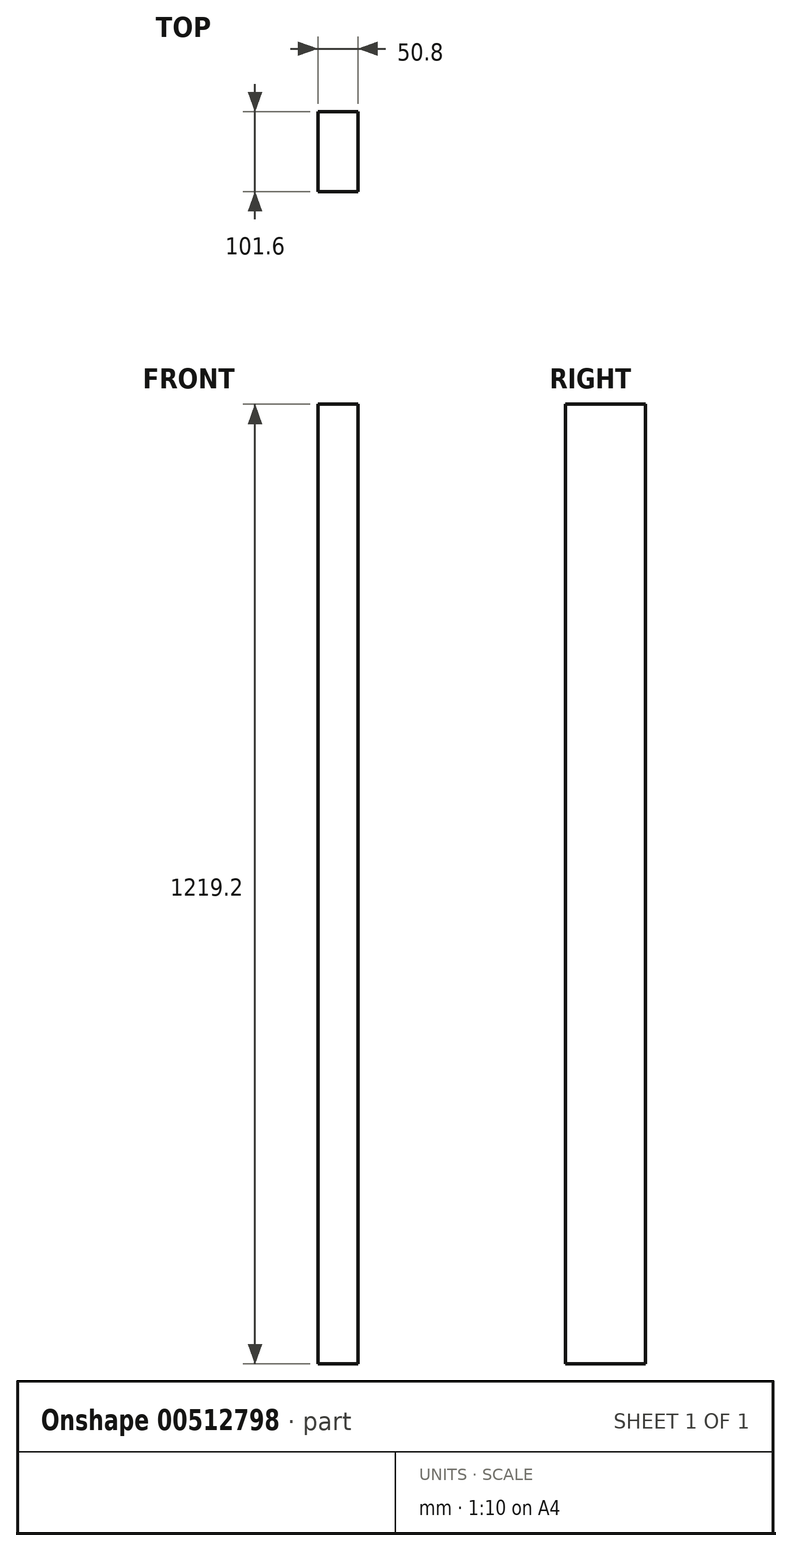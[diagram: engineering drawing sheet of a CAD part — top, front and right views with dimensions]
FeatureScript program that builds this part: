
annotation { "Feature Type Name" : "Feature", "Feature Type Description" : "" }
export const myFeature = defineFeature(function(context is Context, id is Id, definition is map)
    precondition{}
    {
        {
            var Q0;
            Q0=qCreatedBy(makeId("Top.planeOp"),FACE);
            var sketch = newSketch(context, id + "F0", { "sketchPlane" : qUnion([Q0])});
            skLineSegment(sketch, "E0.bottom", {"start": v(-25.4, 50.8) * mm, "end": v(25.4, 50.8) * mm});
            skLineSegment(sketch, "E0.top", {"start": v(-25.4, -50.8) * mm, "end": v(25.4, -50.8) * mm});
            skLineSegment(sketch, "E0.left", {"start": v(-25.4, 50.8) * mm, "end": v(-25.4, -50.8) * mm});
            skLineSegment(sketch, "E0.right", {"start": v(25.4, 50.8) * mm, "end": v(25.4, -50.8) * mm});
            skPoint(sketch, "E0.middle", {"position": v(0, 0) * mm});
            skSolve(sketch);
        }
        {
            var Q0;
            Q0=makeQuery(id+"F0.imprint","IMPRINT",FACE,{"disambiguationData":[TD([[makeQuery(id+"F0.imprint","IMPRINT",EDGE,{"derivedFrom":sQuery(id+"F0.wireOp",EDGE,"E0.bottom")}),-1.0]])]});
            extrude(context, id + "F1", {"entities" : qUnion([Q0]), "depth" : 1219.2 * mm});
        }
    });
